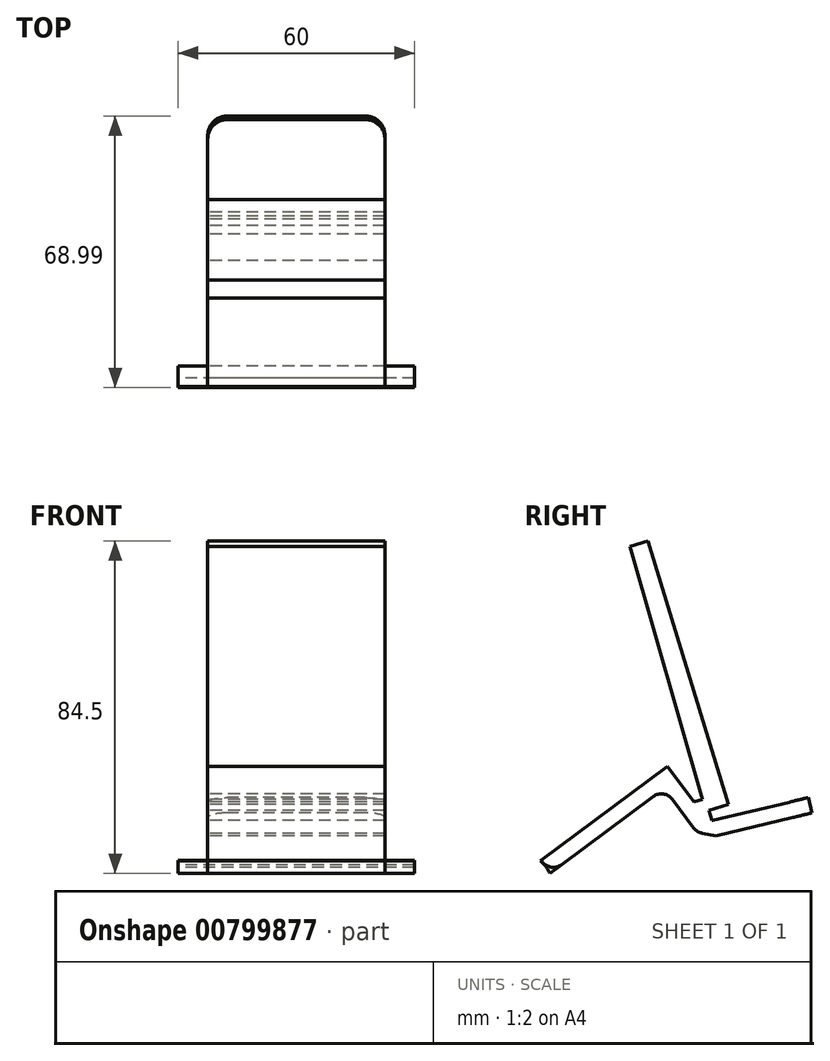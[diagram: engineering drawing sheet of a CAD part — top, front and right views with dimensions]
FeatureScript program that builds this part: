
annotation { "Feature Type Name" : "Feature", "Feature Type Description" : "" }
export const myFeature = defineFeature(function(context is Context, id is Id, definition is map)
    precondition{}
    {
        {
            var Q0;
            Q0=qCreatedBy(makeId("Right.planeOp"),FACE);
            var sketch = newSketch(context, id + "F0", { "sketchPlane" : qUnion([Q0])});
            skCircle(sketch, "E0", {"center": v(6.48, 48.24) * mm, "radius": 7.1 * mm});
            skLineSegment(sketch, "E1", {"start": v(-21.49, -94.36) * mm, "end": v(35.84, 72.05) * mm});
            skLineSegment(sketch, "E2", {"start": v(35.84, 72.05) * mm, "end": v(0.63, 61.96) * mm});
            skLineSegment(sketch, "E3", {"start": v(0.63, 61.96) * mm, "end": v(-56.7, -104.45) * mm});
            skLineSegment(sketch, "E4", {"start": v(-56.7, -104.45) * mm, "end": v(-21.49, -94.36) * mm});
            skLineSegment(sketch, "E5", {"start": v(-56.7, -104.45) * mm, "end": v(-54.5, -112.14) * mm});
            skLineSegment(sketch, "E6", {"start": v(-54.5, -112.14) * mm, "end": v(-16.04, -101.12) * mm});
            skLineSegment(sketch, "E7", {"start": v(-16.04, -101.12) * mm, "end": v(-18.24, -93.43) * mm});
            skLineSegment(sketch, "E8", {"start": v(-18.24, -93.43) * mm, "end": v(-56.7, -104.45) * mm});
            skLineSegment(sketch, "E9", {"start": v(28.71, -103.18) * mm, "end": v(26.81, -92.28) * mm});
            skLineSegment(sketch, "E10", {"start": v(26.81, -92.28) * mm, "end": v(23.86, -92.8) * mm});
            skLineSegment(sketch, "E11", {"start": v(23.86, -92.8) * mm, "end": v(25.76, -103.7) * mm});
            skLineSegment(sketch, "E12", {"start": v(24.2, -106) * mm, "end": v(0.43, -111) * mm});
            skLineSegment(sketch, "E13", {"start": v(-0.78, -110.89) * mm, "end": v(-13.17, -103.41) * mm});
            skLineSegment(sketch, "E14", {"start": v(-13.17, -103.41) * mm, "end": v(-14.72, -105.98) * mm});
            skLineSegment(sketch, "E15", {"start": v(-14.72, -105.98) * mm, "end": v(-2.19, -113.55) * mm});
            skLineSegment(sketch, "E16", {"start": v(1.1, -113.93) * mm, "end": v(24.82, -108.93) * mm});
            skLineSegment(sketch, "E17", {"start": v(-15.21, -104) * mm, "end": v(66.5, -80.57) * mm});
            skLineSegment(sketch, "E18", {"start": v(66.5, -80.57) * mm, "end": v(76.42, -115.17) * mm});
            skLineSegment(sketch, "E19", {"start": v(76.42, -115.17) * mm, "end": v(55.75, -121.1) * mm});
            skLineSegment(sketch, "E20", {"start": v(55.75, -121.1) * mm, "end": v(51.62, -106.68) * mm});
            skLineSegment(sketch, "E21", {"start": v(51.62, -106.68) * mm, "end": v(48.73, -107.5) * mm});
            skLineSegment(sketch, "E22", {"start": v(48.73, -107.5) * mm, "end": v(52.87, -121.93) * mm});
            skArc(sketch, "E23", {"start": v(52.87, -121.93) * mm, "mid": v(54.3, -123.72) * mm, "end": v(56.58, -123.98) * mm});
            skLineSegment(sketch, "E24", {"start": v(56.58, -123.98) * mm, "end": v(77.25, -118.06) * mm});
            skArc(sketch, "E25", {"start": v(77.25, -118.06) * mm, "mid": v(79.04, -116.63) * mm, "end": v(79.3, -114.35) * mm});
            skLineSegment(sketch, "E26", {"start": v(79.3, -114.35) * mm, "end": v(69.38, -79.74) * mm});
            skArc(sketch, "E27", {"start": v(69.38, -79.74) * mm, "mid": v(67.95, -77.94) * mm, "end": v(65.67, -77.68) * mm});
            skLineSegment(sketch, "E28", {"start": v(65.67, -77.68) * mm, "end": v(-16.04, -101.11) * mm});
            skLineSegment(sketch, "E29", {"start": v(-16.04, -101.11) * mm, "end": v(-15.21, -104) * mm});
            skArc(sketch, "E30", {"start": v(-15.21, -104) * mm, "mid": v(-15.9, -105.23) * mm, "end": v(-17.13, -104.55) * mm});
            skArc(sketch, "E31", {"start": v(-17.13, -104.55) * mm, "mid": v(-17.61, -103.95) * mm, "end": v(-18.37, -103.86) * mm});
            skLineSegment(sketch, "E32", {"start": v(-18.37, -103.86) * mm, "end": v(-49.13, -112.68) * mm});
            skArc(sketch, "E33", {"start": v(-49.13, -112.68) * mm, "mid": v(-50.93, -114.11) * mm, "end": v(-51.19, -116.4) * mm});
            skLineSegment(sketch, "E34", {"start": v(-51.19, -116.4) * mm, "end": v(-42.92, -145.23) * mm});
            skArc(sketch, "E35", {"start": v(-42.92, -145.23) * mm, "mid": v(-41.5, -147.03) * mm, "end": v(-39.2, -147.29) * mm});
            skLineSegment(sketch, "E36", {"start": v(-39.2, -147.29) * mm, "end": v(-9.71, -138.83) * mm});
            skLineSegment(sketch, "E37", {"start": v(-9.71, -138.83) * mm, "end": v(-8.48, -139.52) * mm});
            skLineSegment(sketch, "E38", {"start": v(-8.48, -139.52) * mm, "end": v(55.75, -121.1) * mm});
            skLineSegment(sketch, "E39", {"start": v(76.56, -115.65) * mm, "end": v(79.44, -114.83) * mm});
            skLineSegment(sketch, "E40", {"start": v(66.63, -81.05) * mm, "end": v(69.52, -80.22) * mm});
            skLineSegment(sketch, "E41", {"start": v(-37.7, -148.94) * mm, "end": v(-10.78, -141.22) * mm});
            skArc(sketch, "E42", {"start": v(-10.78, -141.22) * mm, "mid": v(-7.19, -138.36) * mm, "end": v(-6.67, -133.8) * mm});
            skLineSegment(sketch, "E43", {"start": v(-6.67, -133.8) * mm, "end": v(-14.39, -106.88) * mm});
            skArc(sketch, "E44", {"start": v(-14.39, -106.88) * mm, "mid": v(-17.24, -103.29) * mm, "end": v(-21.8, -102.77) * mm});
            skLineSegment(sketch, "E45", {"start": v(-21.8, -102.77) * mm, "end": v(-48.72, -110.48) * mm});
            skArc(sketch, "E46", {"start": v(-48.72, -110.48) * mm, "mid": v(-52.32, -113.34) * mm, "end": v(-52.84, -117.9) * mm});
            skLineSegment(sketch, "E47", {"start": v(-52.84, -117.9) * mm, "end": v(-45.12, -144.82) * mm});
            skArc(sketch, "E48", {"start": v(-45.12, -144.82) * mm, "mid": v(-42.26, -148.42) * mm, "end": v(-37.7, -148.94) * mm});
            skLineSegment(sketch, "E49", {"start": v(-38.52, -146.05) * mm, "end": v(-11.6, -138.33) * mm});
            skArc(sketch, "E50", {"start": v(-11.6, -138.33) * mm, "mid": v(-9.81, -136.9) * mm, "end": v(-9.55, -134.62) * mm});
            skLineSegment(sketch, "E51", {"start": v(-9.55, -134.62) * mm, "end": v(-17.27, -107.7) * mm});
            skArc(sketch, "E52", {"start": v(-17.27, -107.7) * mm, "mid": v(-18.7, -105.91) * mm, "end": v(-20.98, -105.65) * mm});
            skLineSegment(sketch, "E53", {"start": v(-20.98, -105.65) * mm, "end": v(-47.9, -113.37) * mm});
            skArc(sketch, "E54", {"start": v(-47.9, -113.37) * mm, "mid": v(-49.7, -114.8) * mm, "end": v(-49.95, -117.08) * mm});
            skLineSegment(sketch, "E55", {"start": v(-49.95, -117.08) * mm, "end": v(-42.23, -144) * mm});
            skArc(sketch, "E56", {"start": v(-42.23, -144) * mm, "mid": v(-40.8, -145.8) * mm, "end": v(-38.52, -146.05) * mm});
            skCircle(sketch, "E57", {"center": v(17.38, -290.23) * mm, "radius": 6.15 * mm});
            skLineSegment(sketch, "E58", {"start": v(25.17, -389.94) * mm, "end": v(-43.46, -150.59) * mm});
            skLineSegment(sketch, "E59", {"start": v(-43.46, -150.59) * mm, "end": v(-5.01, -139.56) * mm});
            skLineSegment(sketch, "E60", {"start": v(-5.01, -139.56) * mm, "end": v(63.62, -378.92) * mm});
            skLineSegment(sketch, "E61", {"start": v(63.62, -378.92) * mm, "end": v(25.17, -389.94) * mm});
            skLineSegment(sketch, "E62", {"start": v(91.44, -382.35) * mm, "end": v(90.52, -378.45) * mm});
            skLineSegment(sketch, "E63", {"start": v(90.52, -378.45) * mm, "end": v(66.13, -384.24) * mm});
            skLineSegment(sketch, "E64", {"start": v(66.13, -384.24) * mm, "end": v(67.06, -388.13) * mm});
            skLineSegment(sketch, "E65", {"start": v(67.06, -388.13) * mm, "end": v(91.44, -382.35) * mm});
            skLineSegment(sketch, "E66", {"start": v(22.64, -394.37) * mm, "end": v(54.73, -370.5) * mm});
            skLineSegment(sketch, "E67", {"start": v(54.73, -370.5) * mm, "end": v(66.67, -386.55) * mm});
            skLineSegment(sketch, "E68", {"start": v(66.67, -386.55) * mm, "end": v(66.27, -386.85) * mm});
            skLineSegment(sketch, "E69", {"start": v(61.37, -386.13) * mm, "end": v(56, -378.9) * mm});
            skLineSegment(sketch, "E70", {"start": v(51.11, -378.19) * mm, "end": v(27.84, -395.5) * mm});
            skLineSegment(sketch, "E71", {"start": v(22.94, -394.77) * mm, "end": v(22.64, -394.37) * mm});
            skCircle(sketch, "E72", {"center": v(17.4, -400.72) * mm, "radius": 5.1 * mm});
            skCircle(sketch, "E73", {"center": v(17.4, -400.72) * mm, "radius": 8 * mm});
            skLineSegment(sketch, "E74", {"start": v(141.28, -440.22) * mm, "end": v(-68.72, -440.22) * mm});
            skLineSegment(sketch, "E75", {"start": v(-68.72, -440.22) * mm, "end": v(-68.72, -434.22) * mm});
            skLineSegment(sketch, "E76", {"start": v(-68.72, -434.22) * mm, "end": v(141.28, -434.22) * mm});
            skLineSegment(sketch, "E77", {"start": v(141.28, -434.22) * mm, "end": v(141.28, -440.22) * mm});
            skLineSegment(sketch, "E78", {"start": v(-1.6, -434.22) * mm, "end": v(81.28, -434.22) * mm});
            skCircle(sketch, "E79", {"center": v(17.38, -290.22) * mm, "radius": 6.1 * mm});
            skLineSegment(sketch, "E80", {"start": v(49.73, -313.25) * mm, "end": v(70.2, -380.19) * mm});
            skLineSegment(sketch, "E81", {"start": v(35.56, -284.7) * mm, "end": v(44.75, -314.77) * mm});
            skLineSegment(sketch, "E82", {"start": v(-1.6, -290.25) * mm, "end": v(-1.6, -434.22) * mm});
            skLineSegment(sketch, "E83", {"start": v(70.2, -380.19) * mm, "end": v(65.22, -381.7) * mm});
            skLineSegment(sketch, "E84", {"start": v(49.73, -313.25) * mm, "end": v(44.75, -314.77) * mm});
            skLineSegment(sketch, "E85", {"start": v(65.22, -381.7) * mm, "end": v(81.28, -434.22) * mm});
            skArc(sketch, "E86", {"start": v(35.56, -284.7) * mm, "mid": v(14.58, -271.46) * mm, "end": v(-1.6, -290.25) * mm});
            skLineSegment(sketch, "E87", {"start": v(38.16, -434.22) * mm, "end": v(32.5, -434.22) * mm});
            skCircle(sketch, "E88", {"center": v(6.48, 48.24) * mm, "radius": 4.65 * mm});
            skArc(sketch, "E89", {"start": v(4.1, 71) * mm, "mid": v(-20.52, 166.4) * mm, "end": v(-44.39, 262) * mm});
            skArc(sketch, "E90", {"start": v(-44.39, 262) * mm, "mid": v(-44.59, 263.23) * mm, "end": v(-44.6, 264.49) * mm});
            skArc(sketch, "E91", {"start": v(-44.6, 264.49) * mm, "mid": v(-39.9, 276.32) * mm, "end": v(-29.25, 283.32) * mm});
            skArc(sketch, "E92", {"start": v(-29.25, 283.32) * mm, "mid": v(-17.73, 285.43) * mm, "end": v(-6.06, 286.48) * mm});
            skArc(sketch, "E93", {"start": v(-6.06, 286.48) * mm, "mid": v(-5.1, 286.44) * mm, "end": v(-4.17, 286.3) * mm});
            skArc(sketch, "E94", {"start": v(-4.17, 286.3) * mm, "mid": v(2.63, 283) * mm, "end": v(7.16, 276.96) * mm});
            skArc(sketch, "E95", {"start": v(7.16, 276.96) * mm, "mid": v(68.43, 63) * mm, "end": v(93.98, -158.07) * mm});
            skArc(sketch, "E96", {"start": v(93.98, -158.07) * mm, "mid": v(93.1, -162.74) * mm, "end": v(90.7, -166.84) * mm});
            skArc(sketch, "E97", {"start": v(90.7, -166.84) * mm, "mid": v(88.8, -168.52) * mm, "end": v(86.45, -169.46) * mm});
            skArc(sketch, "E98", {"start": v(86.45, -169.46) * mm, "mid": v(86.26, -169.5) * mm, "end": v(86.07, -169.56) * mm});
            skArc(sketch, "E99", {"start": v(86.07, -169.56) * mm, "mid": v(66.91, -173.7) * mm, "end": v(47.35, -174.98) * mm});
            skArc(sketch, "E100", {"start": v(47.35, -174.98) * mm, "mid": v(43.94, -174.64) * mm, "end": v(40.54, -174.21) * mm});
            skArc(sketch, "E101", {"start": v(40.54, -174.21) * mm, "mid": v(28.25, -167.76) * mm, "end": v(20.25, -156.43) * mm});
            skArc(sketch, "E102", {"start": v(20.25, -156.43) * mm, "mid": v(18.93, -150.12) * mm, "end": v(18.81, -143.67) * mm});
            skArc(sketch, "E103", {"start": v(18.81, -143.67) * mm, "mid": v(19.6, -117.3) * mm, "end": v(19.59, -90.9) * mm});
            skArc(sketch, "E104", {"start": v(19.59, -90.9) * mm, "mid": v(19.78, -29.41) * mm, "end": v(13.92, 31.8) * mm});
            skArc(sketch, "E105", {"start": v(13.92, 31.8) * mm, "mid": v(9.66, 51.56) * mm, "end": v(4.1, 71) * mm});
            skArc(sketch, "E106", {"start": v(-137.69, 424.9) * mm, "mid": v(-147.3, 434.61) * mm, "end": v(-160.05, 439.54) * mm});
            skArc(sketch, "E107", {"start": v(-160.05, 439.54) * mm, "mid": v(-180.78, 439.22) * mm, "end": v(-200.34, 432.34) * mm});
            skArc(sketch, "E108", {"start": v(-200.34, 432.34) * mm, "mid": v(-204.9, 427.92) * mm, "end": v(-206.12, 421.67) * mm});
            skArc(sketch, "E109", {"start": v(-206.12, 421.67) * mm, "mid": v(-206, 420.94) * mm, "end": v(-205.82, 420.23) * mm});
            skLineSegment(sketch, "E110", {"start": v(-205.82, 420.23) * mm, "end": v(-58.23, -94.57) * mm});
            skArc(sketch, "E111", {"start": v(-58.23, -94.57) * mm, "mid": v(-53.46, -100.55) * mm, "end": v(-45.86, -101.41) * mm});
            skLineSegment(sketch, "E112", {"start": v(-45.86, -101.41) * mm, "end": v(5.9, -86.37) * mm});
            skArc(sketch, "E113", {"start": v(5.9, -86.37) * mm, "mid": v(10.21, -83.84) * mm, "end": v(12.76, -79.54) * mm});
            skArc(sketch, "E114", {"start": v(12.76, -79.54) * mm, "mid": v(17.43, -17.67) * mm, "end": v(9.23, 43.83) * mm});
            skLineSegment(sketch, "E115", {"start": v(9.23, 43.83) * mm, "end": v(-9.5, 110.77) * mm});
            skArc(sketch, "E116", {"start": v(-9.5, 110.77) * mm, "mid": v(-9.84, 111.87) * mm, "end": v(-10.24, 112.95) * mm});
            skLineSegment(sketch, "E117", {"start": v(-10.24, 112.95) * mm, "end": v(-137.69, 424.9) * mm});
            skFitSpline(sketch, "E118", {"points": [v(-154.98, 438.3) * mm, v(-149.65, 423.02) * mm, v(-138.88, 392.17) * mm, v(-123.48, 347.85) * mm, v(-106.67, 299.55) * mm, v(-90.33, 252.57) * mm, v(-72.98, 202.7) * mm, v(-56.87, 156.4) * mm, v(-39.13, 105.36) * mm, v(-24.8, 64.39) * mm, v(-9.08, 20.28) * mm, v(1.89, -26.42) * mm, v(0.65, -67.31) * mm, v(0.02, -88.1) * mm]});
            skLineSegment(sketch, "E119", {"start": v(-151.8, 431.49) * mm, "end": v(-153.65, 437.84) * mm});
            skLineSegment(sketch, "E120", {"start": v(73.3, 77.6) * mm, "end": v(195.04, 137.67) * mm});
            skLineSegment(sketch, "E121", {"start": v(-55.5, 65.87) * mm, "end": v(-55.23, 62.88) * mm});
            skLineSegment(sketch, "E122", {"start": v(-55.23, 62.88) * mm, "end": v(-43.66, 63.88) * mm});
            skLineSegment(sketch, "E123", {"start": v(-43.66, 63.88) * mm, "end": v(70.6, 73.7) * mm});
            skArc(sketch, "E124", {"start": v(70.6, 73.7) * mm, "mid": v(72.4, 74.02) * mm, "end": v(74.1, 74.67) * mm});
            skLineSegment(sketch, "E125", {"start": v(74.1, 74.67) * mm, "end": v(196.3, 134.94) * mm});
            skLineSegment(sketch, "E126", {"start": v(69.78, 76.64) * mm, "end": v(-55.5, 65.87) * mm});
            skArc(sketch, "E127", {"start": v(69.78, 76.64) * mm, "mid": v(71.58, 76.96) * mm, "end": v(73.3, 77.6) * mm});
            skArc(sketch, "E128", {"start": v(-17.47, 47.75) * mm, "mid": v(-2, 37.82) * mm, "end": v(15, 30.89) * mm});
            skArc(sketch, "E129", {"start": v(-37.08, 63.06) * mm, "mid": v(-40.86, 63.82) * mm, "end": v(-44.72, 63.78) * mm});
            skArc(sketch, "E130", {"start": v(-44.98, 66.77) * mm, "mid": v(-41.08, 65.8) * mm, "end": v(-37.74, 63.58) * mm});
            skLineSegment(sketch, "E131", {"start": v(-37.74, 63.58) * mm, "end": v(-17.47, 47.75) * mm});
            skLineSegment(sketch, "E132", {"start": v(34.99, 24.82) * mm, "end": v(15, 30.89) * mm});
            skArc(sketch, "E133", {"start": v(40.23, 26.34) * mm, "mid": v(57.09, 48.94) * mm, "end": v(70.6, 73.7) * mm});
            skArc(sketch, "E134", {"start": v(34.99, 24.82) * mm, "mid": v(37.83, 24.8) * mm, "end": v(40.23, 26.34) * mm});
            skArc(sketch, "E135", {"start": v(41.36, 25.36) * mm, "mid": v(58.63, 48.57) * mm, "end": v(72.39, 74.02) * mm});
            skLineSegment(sketch, "E136", {"start": v(41.36, 25.36) * mm, "end": v(40.23, 26.34) * mm});
            skLineSegment(sketch, "E137", {"start": v(-71.53, 64.48) * mm, "end": v(71.6, 76.97) * mm});
            skLineSegment(sketch, "E138", {"start": v(71.6, 76.97) * mm, "end": v(193.05, 136.7) * mm});
            skArc(sketch, "E139", {"start": v(193.05, 136.7) * mm, "mid": v(194.9, 137.87) * mm, "end": v(196.45, 139.43) * mm});
            skLineSegment(sketch, "E140", {"start": v(196.45, 139.43) * mm, "end": v(204, 148.88) * mm});
            skArc(sketch, "E141", {"start": v(204, 148.88) * mm, "mid": v(205, 159.84) * mm, "end": v(195.32, 165.08) * mm});
            skLineSegment(sketch, "E142", {"start": v(195.32, 165.08) * mm, "end": v(-20.71, 144.05) * mm});
            skArc(sketch, "E143", {"start": v(-20.71, 144.05) * mm, "mid": v(-31.4, 142.57) * mm, "end": v(-41.83, 139.81) * mm});
            skArc(sketch, "E144", {"start": v(-41.83, 139.81) * mm, "mid": v(-43.58, 139.04) * mm, "end": v(-45.15, 137.96) * mm});
            skArc(sketch, "E145", {"start": v(-45.15, 137.96) * mm, "mid": v(-68.51, 110.65) * mm, "end": v(-81.98, 77.32) * mm});
            skArc(sketch, "E146", {"start": v(-81.98, 77.32) * mm, "mid": v(-80.16, 68.13) * mm, "end": v(-71.53, 64.48) * mm});
            skArc(sketch, "E147", {"start": v(-2.19, -113.55) * mm, "mid": v(-0.57, -114.02) * mm, "end": v(1.1, -113.93) * mm});
            skArc(sketch, "E148", {"start": v(24.82, -108.93) * mm, "mid": v(27.93, -106.85) * mm, "end": v(28.71, -103.18) * mm});
            skArc(sketch, "E149", {"start": v(24.2, -106) * mm, "mid": v(25.44, -105.16) * mm, "end": v(25.76, -103.7) * mm});
            skArc(sketch, "E150", {"start": v(-0.78, -110.89) * mm, "mid": v(-0.19, -111.04) * mm, "end": v(0.43, -111) * mm});
            skArc(sketch, "E151", {"start": v(22.94, -394.77) * mm, "mid": v(25.24, -396.15) * mm, "end": v(27.84, -395.5) * mm});
            skArc(sketch, "E152", {"start": v(56, -378.9) * mm, "mid": v(53.7, -377.54) * mm, "end": v(51.11, -378.19) * mm});
            skArc(sketch, "E153", {"start": v(61.37, -386.13) * mm, "mid": v(63.67, -387.5) * mm, "end": v(66.27, -386.85) * mm});
            skLineSegment(sketch, "E154", {"start": v(22.64, -394.37) * mm, "end": v(22.44, -394.52) * mm});
            skLineSegment(sketch, "E155", {"start": v(27.84, -395.5) * mm, "end": v(24.82, -397.75) * mm});
            skLineSegment(sketch, "E156", {"start": v(66.13, -384.24) * mm, "end": v(65.13, -384.47) * mm});
            skLineSegment(sketch, "E157", {"start": v(67.06, -388.13) * mm, "end": v(63.55, -387.48) * mm});
            skSolve(sketch);
        }
        {
            var Q0;
            Q0=makeQuery(id+"F0.imprint","IMPRINT",FACE,{"disambiguationData":[TD([[makeQuery(id+"F0.imprint","IMPRINT",EDGE,{"derivedFrom":sQuery(id+"F0.wireOp",EDGE,"E73")}),-1.0]])]});
            extrude(context, id + "F1", {"entities" : qUnion([Q0]), "endBound" : BoundingType.SYMMETRIC, "depth" : 60 * mm, "offsetDistance" : 25 * mm});
        }
        {
            var Q0;
            {var subQ0=sQuery(id+"F0.wireOp",EDGE,"E71");Q0=makeQuery(id+"F0.imprint","IMPRINT",FACE,{"disambiguationData":[TD([[makeQuery(id+"F0.imprint","IMPRINT",EDGE,{"derivedFrom":subQ0}),-1.0]])]});}
            var Q1;
            {var subQ10=sQuery(id+"F0.wireOp",EDGE,"E152");Q1=makeQuery(id+"F0.imprint","IMPRINT",FACE,{"disambiguationData":[TD([[makeQuery(id+"F0.imprint","IMPRINT",EDGE,{"derivedFrom":subQ10}),-1.0]])]});}
            var Q2;
            {var subQ0=sQuery(id+"F0.wireOp",EDGE,"E68");Q2=makeQuery(id+"F0.imprint","IMPRINT",FACE,{"disambiguationData":[TD([[makeQuery(id+"F0.imprint","IMPRINT",EDGE,{"derivedFrom":subQ0}),-1.0]])]});}
            var Q3;
            {var subQ6=sQuery(id+"F0.wireOp",EDGE,"E62");Q3=makeQuery(id+"F0.imprint","IMPRINT",FACE,{"disambiguationData":[TD([[makeQuery(id+"F0.imprint","IMPRINT",EDGE,{"derivedFrom":subQ6}),1.0]])]});}
            var Q4;
            {var subQ6=sQuery(id+"F0.wireOp",EDGE,"E68");Q4=makeQuery(id+"F0.imprint","IMPRINT",FACE,{"disambiguationData":[TD([[makeQuery(id+"F0.imprint","IMPRINT",EDGE,{"derivedFrom":subQ6}),1.0]])]});}
            var Q5;
            {var subQ0=sQuery(id+"F0.wireOp",EDGE,"E156");var subQ3=sQuery(id+"F0.wireOp",EDGE,"E85");var subQ5=makeQuery(id+"F0.imprint","INTERSECT",VERTEX,{"derivedFrom":[subQ3,subQ0]});Q5=makeQuery(id+"F0.imprint","IMPRINT",FACE,{"disambiguationData":[TD([[makeQuery(id+"F0.imprint","IMPRINT",EDGE,{"disambiguationData":[TD([[subQ5,-1.0]])],"derivedFrom":subQ3}),1.0]])]});}
            var Q6;
            {var subQ0=sQuery(id+"F0.wireOp",EDGE,"E65");var subQ3=sQuery(id+"F0.wireOp",EDGE,"E85");var subQ5=makeQuery(id+"F0.imprint","INTERSECT",VERTEX,{"derivedFrom":[subQ0,subQ3]});Q6=makeQuery(id+"F0.imprint","IMPRINT",FACE,{"disambiguationData":[TD([[makeQuery(id+"F0.imprint","IMPRINT",EDGE,{"disambiguationData":[TD([[subQ5,1.0]])],"derivedFrom":subQ3}),-1.0]])]});}
            var Q7;
            Q7=makeQuery(id+"F0.imprint","IMPRINT",FACE,{"disambiguationData":[TD([[makeQuery(id+"F0.imprint","IMPRINT",EDGE,{"derivedFrom":sQuery(id+"F0.wireOp",EDGE,"E71")}),1.0]])]});
            extrude(context, id + "F2", {"entities" : qUnion([Q0, Q1, Q2, Q3, Q4, Q5, Q6, Q7]), "endBound" : BoundingType.SYMMETRIC, "depth" : 45 * mm, "offsetDistance" : 25 * mm});
        }
        {
            var Q0;
            Q0=makeQuery(id+"F2.opExtrude","CAP_EDGE",EDGE,{"disambiguationData":[OSD([sQuery(id+"F0.wireOp",EDGE,"E62")])],"isStart":false});
            var Q1;
            Q1=makeQuery(id+"F2.opExtrude","CAP_EDGE",EDGE,{"disambiguationData":[OSD([sQuery(id+"F0.wireOp",EDGE,"E62")])],"isStart":true});
            fillet(context, id + "F3", {"entities" : qUnion([Q0, Q1]), "radius" : 5 * mm, "tangentPropagation" : true, "allowEdgeOverflow" : false});
        }
    });
